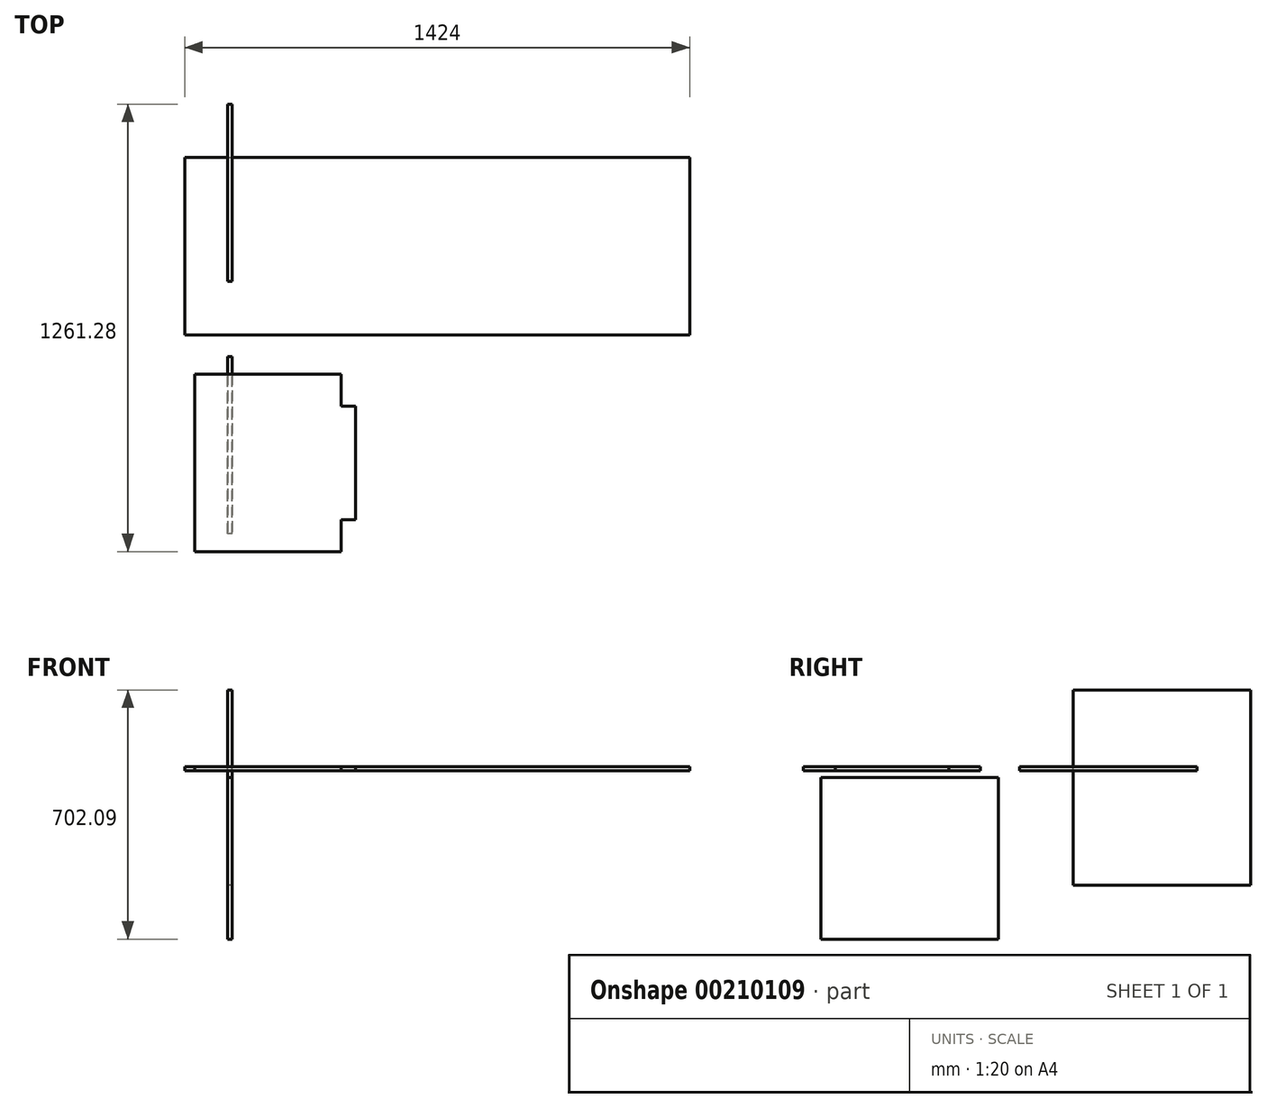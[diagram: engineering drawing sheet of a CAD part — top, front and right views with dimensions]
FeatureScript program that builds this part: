
annotation { "Feature Type Name" : "Feature", "Feature Type Description" : "" }
export const myFeature = defineFeature(function(context is Context, id is Id, definition is map)
    precondition{}
    {
        {
            var Q0;
            Q0=qCreatedBy(makeId("Top.planeOp"),FACE);
            var sketch = newSketch(context, id + "F0", { "sketchPlane" : qUnion([Q0])});
            skLineSegment(sketch, "E0", {"start": v(-121.41, -40) * mm, "end": v(-121.41, 460) * mm});
            skLineSegment(sketch, "E1", {"start": v(-121.41, 460) * mm, "end": v(1302.59, 460) * mm});
            skLineSegment(sketch, "E2", {"start": v(1302.59, 460) * mm, "end": v(1302.59, -40) * mm});
            skLineSegment(sketch, "E3", {"start": v(1302.59, -40) * mm, "end": v(-121.41, -40) * mm});
            skSolve(sketch);
        }
        {
            var Q0;
            Q0 = qSketchRegion(id + "F0", true);
            extrude(context, id + "F1", {"entities" : qUnion([Q0]), "depth" : 12 * mm});
        }
        {
            var Q0;
            Q0=qCreatedBy(makeId("Right.planeOp"),FACE);
            var sketch = newSketch(context, id + "F2", { "sketchPlane" : qUnion([Q0])});
            skLineSegment(sketch, "E4", {"start": v(610.92, -321.84) * mm, "end": v(110.92, -321.84) * mm});
            skLineSegment(sketch, "E5", {"start": v(110.92, -321.84) * mm, "end": v(110.92, 228.16) * mm});
            skLineSegment(sketch, "E6", {"start": v(110.92, 228.16) * mm, "end": v(610.92, 228.16) * mm});
            skLineSegment(sketch, "E7", {"start": v(610.92, 228.16) * mm, "end": v(610.92, -321.84) * mm});
            skSolve(sketch);
        }
        {
            var Q0;
            Q0 = qSketchRegion(id + "F2", true);
            extrude(context, id + "F3", {"entities" : qUnion([Q0]), "depth" : 12 * mm});
        }
        {
            var Q0;
            Q0=qCreatedBy(makeId("Top.planeOp"),FACE);
            var sketch = newSketch(context, id + "F4", { "sketchPlane" : qUnion([Q0])});
            skLineSegment(sketch, "E8", {"start": v(-92.51, -150.36) * mm, "end": v(319.49, -150.36) * mm});
            skLineSegment(sketch, "E9", {"start": v(-92.51, -650.36) * mm, "end": v(-92.51, -150.36) * mm});
            skLineSegment(sketch, "E10", {"start": v(360.49, -240.36) * mm, "end": v(360.49, -560.36) * mm});
            skLineSegment(sketch, "E11", {"start": v(319.49, -650.36) * mm, "end": v(-92.51, -650.36) * mm});
            skLineSegment(sketch, "E12", {"start": v(360.49, -240.36) * mm, "end": v(319.49, -240.36) * mm});
            skLineSegment(sketch, "E13", {"start": v(319.49, -240.36) * mm, "end": v(319.49, -150.36) * mm});
            skLineSegment(sketch, "E14", {"start": v(319.49, -650.36) * mm, "end": v(319.49, -560.36) * mm});
            skLineSegment(sketch, "E15", {"start": v(319.49, -560.36) * mm, "end": v(360.49, -560.36) * mm});
            skSolve(sketch);
        }
        {
            var Q0;
            Q0 = qSketchRegion(id + "F4", true);
            extrude(context, id + "F5", {"entities" : qUnion([Q0]), "depth" : 12 * mm});
        }
        {
            var Q0;
            Q0=qCreatedBy(makeId("Right.planeOp"),FACE);
            var sketch = newSketch(context, id + "F6", { "sketchPlane" : qUnion([Q0])});
            skLineSegment(sketch, "E16", {"start": v(-100.56, -17.93) * mm, "end": v(-600.56, -17.93) * mm});
            skLineSegment(sketch, "E17", {"start": v(-600.56, -17.93) * mm, "end": v(-600.56, -473.93) * mm});
            skLineSegment(sketch, "E18", {"start": v(-600.56, -473.93) * mm, "end": v(-100.56, -473.93) * mm});
            skLineSegment(sketch, "E19", {"start": v(-100.56, -473.93) * mm, "end": v(-100.56, -17.93) * mm});
            skSolve(sketch);
        }
        {
            var Q0;
            Q0 = qSketchRegion(id + "F6", true);
            extrude(context, id + "F7", {"entities" : qUnion([Q0]), "depth" : 12 * mm});
        }
    });
